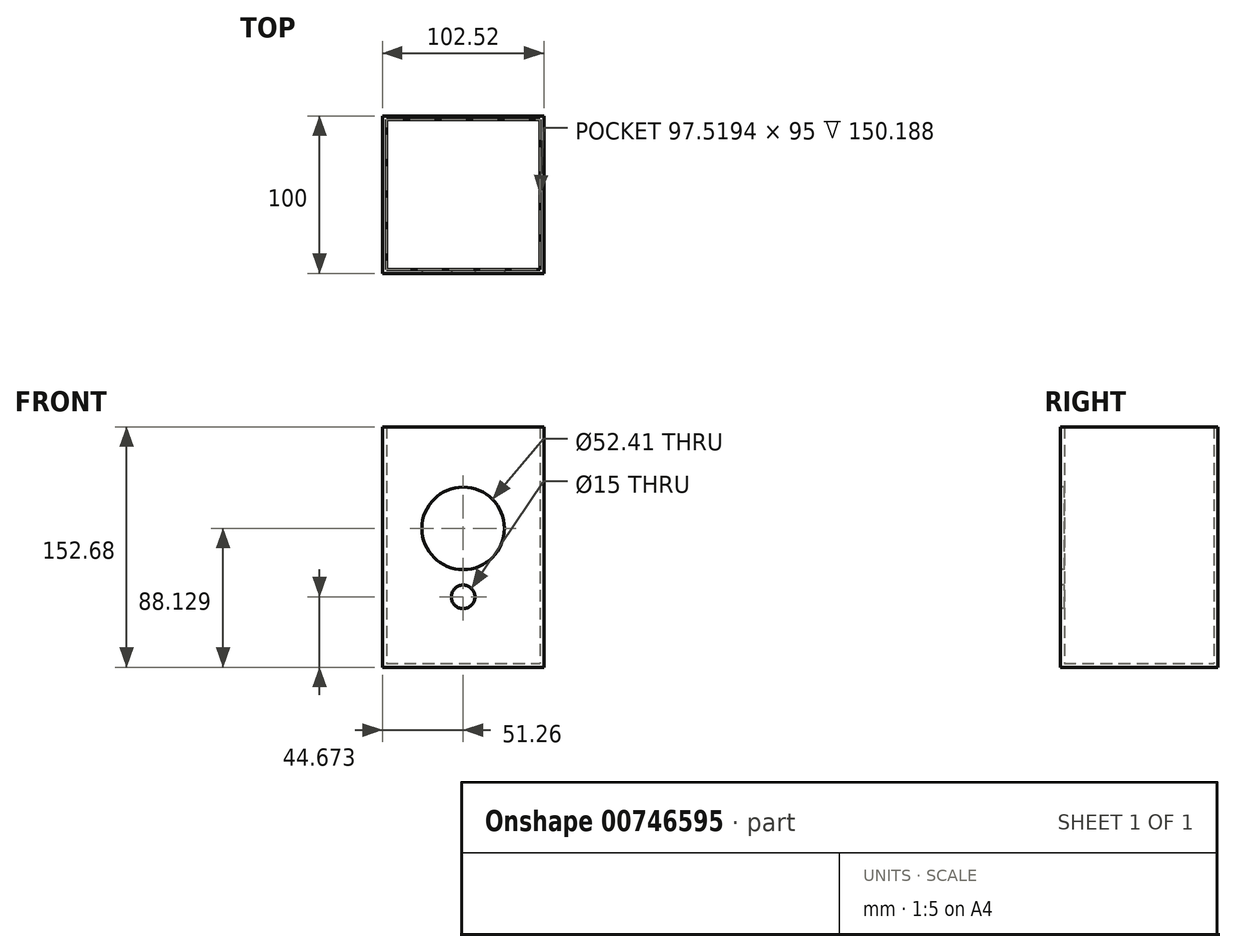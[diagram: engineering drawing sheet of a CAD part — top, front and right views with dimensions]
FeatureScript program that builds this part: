
annotation { "Feature Type Name" : "Feature", "Feature Type Description" : "" }
export const myFeature = defineFeature(function(context is Context, id is Id, definition is map)
    precondition{}
    {
        {
            var Q0;
            Q0=qCreatedBy(makeId("Front.planeOp"),FACE);
            var sketch = newSketch(context, id + "F0", { "sketchPlane" : qUnion([Q0])});
            skLineSegment(sketch, "E0.bottom", {"start": v(-51.26, 76.34) * mm, "end": v(51.26, 76.34) * mm});
            skLineSegment(sketch, "E0.top", {"start": v(-51.26, -76.34) * mm, "end": v(51.26, -76.34) * mm});
            skLineSegment(sketch, "E0.left", {"start": v(-51.26, 76.34) * mm, "end": v(-51.26, -76.34) * mm});
            skLineSegment(sketch, "E0.right", {"start": v(51.26, 76.34) * mm, "end": v(51.26, -76.34) * mm});
            skPoint(sketch, "E0.middle", {"position": v(0, 0) * mm});
            skSolve(sketch);
        }
        {
            var Q0;
            Q0 = qSketchRegion(id + "F0", true);
            extrude(context, id + "F1", {"entities" : qUnion([Q0]), "depth" : 100 * mm, "offsetDistance" : 25 * mm});
        }
        {
            var Q0;
            Q0=makeQuery(id+"F1.opExtrude","SWEPT_FACE",FACE,{"disambiguationData":[OSD([sQuery(id+"F0.wireOp",EDGE,"E0.bottom")])]});
            shell(context, id + "F2", {"entities" : qUnion([Q0]), "thickness" : 2.5 * mm});
        }
        {
            var Q0;
            Q0=makeQuery(id+"F1.opExtrude","CAP_FACE",FACE,{"disambiguationData":[OSD([sQuery(id+"F0.wireOp",EDGE,"E0.bottom"),sQuery(id+"F0.wireOp",EDGE,"E0.top"),sQuery(id+"F0.wireOp",EDGE,"E0.left"),sQuery(id+"F0.wireOp",EDGE,"E0.right")])],"isStart":false});
            var sketch = newSketch(context, id + "F3", { "sketchPlane" : qUnion([Q0])});
            skCircle(sketch, "E1", {"center": v(0, 11.79) * mm, "radius": 26.2 * mm});
            skSolve(sketch);
        }
        {
            var Q0;
            Q0 = qSketchRegion(id + "F3", true);
            extrude(context, id + "F4", {"entities" : qUnion([Q0]), "operationType" : NewBodyOperationType.REMOVE, "oppositeDirection" : true, "depth" : 25 * mm, "offsetDistance" : 25 * mm});
        }
        {
            var Q0;
            Q0=makeQuery(id+"F1.opExtrude","CAP_FACE",FACE,{"disambiguationData":[OSD([sQuery(id+"F0.wireOp",EDGE,"E0.bottom"),sQuery(id+"F0.wireOp",EDGE,"E0.top"),sQuery(id+"F0.wireOp",EDGE,"E0.left"),sQuery(id+"F0.wireOp",EDGE,"E0.right")])],"isStart":false});
            var sketch = newSketch(context, id + "F5", { "sketchPlane" : qUnion([Q0])});
            skCircle(sketch, "E2", {"center": v(0, -31.67) * mm, "radius": 7.5 * mm});
            skSolve(sketch);
        }
        {
            var Q0;
            Q0 = qSketchRegion(id + "F5", true);
            extrude(context, id + "F6", {"entities" : qUnion([Q0]), "operationType" : NewBodyOperationType.REMOVE, "oppositeDirection" : true, "depth" : 25 * mm, "offsetDistance" : 25 * mm});
        }
    });
